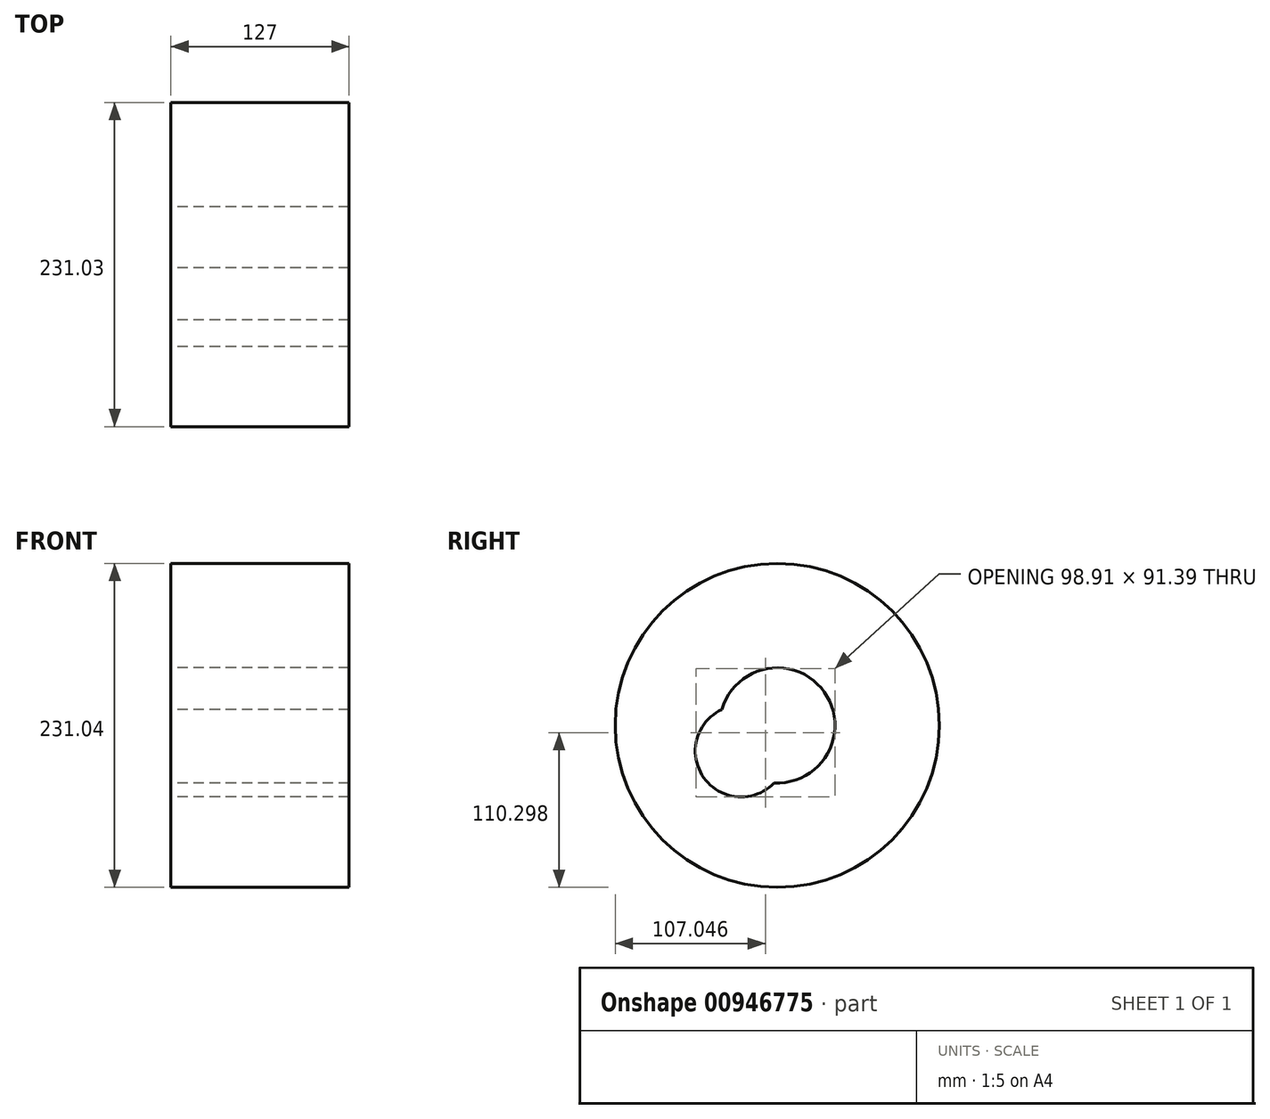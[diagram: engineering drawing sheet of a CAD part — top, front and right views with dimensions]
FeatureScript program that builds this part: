
annotation { "Feature Type Name" : "Feature", "Feature Type Description" : "" }
export const myFeature = defineFeature(function(context is Context, id is Id, definition is map)
    precondition{}
    {
        {
            var Q0;
            Q0=qCreatedBy(makeId("Right.planeOp"),FACE);
            var sketch = newSketch(context, id + "F0", { "sketchPlane" : qUnion([Q0])});
            skCircle(sketch, "E0", {"center": v(-50.33, 49.48) * mm, "radius": 32.68 * mm});
            skCircle(sketch, "E1", {"center": v(-24.56, 67.8) * mm, "radius": 41.06 * mm});
            skCircle(sketch, "E2", {"center": v(-24.56, 67.8) * mm, "radius": 115.52 * mm});
            skSolve(sketch);
        }
        {
            var Q0;
            Q0=makeQuery(id+"F0.imprint","IMPRINT",FACE,{"disambiguationData":[TD([[makeQuery(id+"F0.imprint","IMPRINT",EDGE,{"derivedFrom":sQuery(id+"F0.wireOp",EDGE,"E2")}),1.0]])]});
            extrude(context, id + "F1", {"entities" : qUnion([Q0]), "depth" : 127 * mm, "offsetDistance" : 25.4 * mm});
        }
    });
